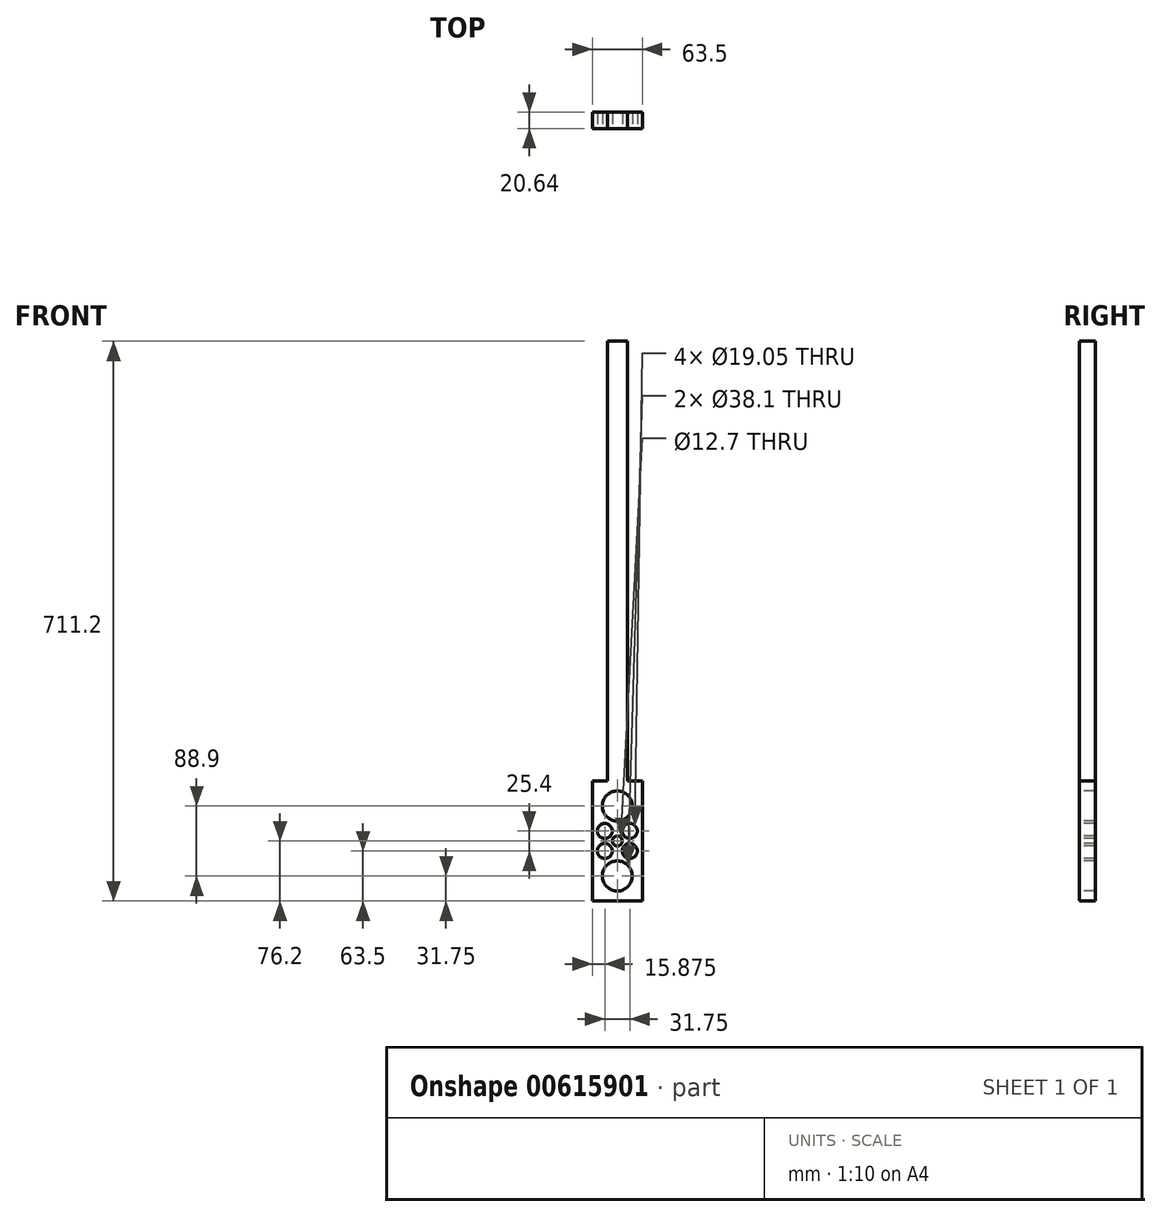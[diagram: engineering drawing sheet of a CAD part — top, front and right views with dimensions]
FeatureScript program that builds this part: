
annotation { "Feature Type Name" : "Feature", "Feature Type Description" : "" }
export const myFeature = defineFeature(function(context is Context, id is Id, definition is map)
    precondition{}
    {
        {
            var Q0;
            Q0=qCreatedBy(makeId("Front.planeOp"),FACE);
            var sketch = newSketch(context, id + "F0", { "sketchPlane" : qUnion([Q0])});
            skLineSegment(sketch, "E0.bottom", {"start": v(0, 0) * mm, "end": v(-63.5, 0) * mm});
            skLineSegment(sketch, "E0.top", {"start": v(0, 152.4) * mm, "end": v(-63.5, 152.4) * mm});
            skLineSegment(sketch, "E0.left", {"start": v(0, 0) * mm, "end": v(0, 152.4) * mm});
            skLineSegment(sketch, "E0.right", {"start": v(-63.5, 0) * mm, "end": v(-63.5, 152.4) * mm});
            skLineSegment(sketch, "E1.bottom", {"start": v(-31.75, 152.4) * mm, "end": v(-44.45, 152.4) * mm});
            skLineSegment(sketch, "E1.top", {"start": v(-31.75, 711.2) * mm, "end": v(-44.45, 711.2) * mm});
            skLineSegment(sketch, "E1.left", {"start": v(-31.75, 152.4) * mm, "end": v(-31.75, 711.2) * mm});
            skLineSegment(sketch, "E1.right", {"start": v(-44.45, 152.4) * mm, "end": v(-44.45, 711.2) * mm});
            skLineSegment(sketch, "E2.bottom", {"start": v(-31.75, 152.4) * mm, "end": v(-19.05, 152.4) * mm});
            skLineSegment(sketch, "E2.top", {"start": v(-31.75, 711.2) * mm, "end": v(-19.05, 711.2) * mm});
            skLineSegment(sketch, "E2.right", {"start": v(-19.05, 152.4) * mm, "end": v(-19.05, 711.2) * mm});
            skSolve(sketch);
        }
        {
            var Q0;
            Q0 = qSketchRegion(id + "F0", true);
            extrude(context, id + "F1", {"entities" : qUnion([Q0]), "depth" : 20.64 * mm, "offsetDistance" : 25.4 * mm});
        }
        {
            var Q0;
            Q0=makeQuery(id+"F1.opExtrude","CAP_FACE",FACE,{"disambiguationData":[OSD([sQuery(id+"F0.wireOp",EDGE,"E0.bottom"),sQuery(id+"F0.wireOp",EDGE,"E0.top"),sQuery(id+"F0.wireOp",EDGE,"E0.left"),sQuery(id+"F0.wireOp",EDGE,"E0.right"),sQuery(id+"F0.wireOp",EDGE,"E1.top"),sQuery(id+"F0.wireOp",EDGE,"E1.right"),sQuery(id+"F0.wireOp",EDGE,"E2.top"),sQuery(id+"F0.wireOp",EDGE,"E2.right")])],"isStart":false});
            var sketch = newSketch(context, id + "F2", { "sketchPlane" : qUnion([Q0])});
            skLineSegment(sketch, "E3", {"start": v(0, 0) * mm, "end": v(-31.75, 0) * mm});
            skLineSegment(sketch, "E4", {"start": v(-31.75, 0) * mm, "end": v(-31.75, 31.75) * mm, "construction": true});
            skCircle(sketch, "E5", {"center": v(-31.75, 31.75) * mm, "radius": 19.05 * mm});
            skLineSegment(sketch, "E6", {"start": v(0, 0) * mm, "end": v(-15.88, 0) * mm});
            skLineSegment(sketch, "E7", {"start": v(-15.88, 0) * mm, "end": v(-15.88, 63.5) * mm, "construction": true});
            skLineSegment(sketch, "E8", {"start": v(-63.5, 0) * mm, "end": v(-47.62, 0) * mm});
            skLineSegment(sketch, "E9", {"start": v(-47.62, 0) * mm, "end": v(-47.62, 63.5) * mm, "construction": true});
            skCircle(sketch, "E10", {"center": v(-47.63, 63.5) * mm, "radius": 9.53 * mm});
            skCircle(sketch, "E11", {"center": v(-15.88, 63.5) * mm, "radius": 9.53 * mm});
            skLineSegment(sketch, "E12", {"start": v(-63.5, 0) * mm, "end": v(-55.56, 0) * mm});
            skLineSegment(sketch, "E13", {"start": v(0, 0) * mm, "end": v(-7.94, 0) * mm});
            skLineSegment(sketch, "E14", {"start": v(-31.75, 0) * mm, "end": v(-23.81, 0) * mm});
            skLineSegment(sketch, "E15", {"start": v(-31.75, 0) * mm, "end": v(-39.69, 0) * mm});
            skLineSegment(sketch, "E16", {"start": v(-63.5, 0) * mm, "end": v(-42.33, 0) * mm});
            skLineSegment(sketch, "E17", {"start": v(0, 0) * mm, "end": v(-21.17, 0) * mm});
            skLineSegment(sketch, "E18", {"start": v(-31.75, 0) * mm, "end": v(-31.75, 57.15) * mm, "construction": true});
            skLineSegment(sketch, "E19", {"start": v(0, 0) * mm, "end": v(0, 76.2) * mm});
            skLineSegment(sketch, "E20", {"start": v(0, 76.2) * mm, "end": v(-63.5, 76.2) * mm});
            skCircle(sketch, "E21.MirrorC", {"center": v(-47.63, 88.9) * mm, "radius": 9.53 * mm});
            skCircle(sketch, "E22.MirrorC", {"center": v(-15.88, 88.9) * mm, "radius": 9.53 * mm});
            skCircle(sketch, "E23.MirrorC", {"center": v(-31.75, 120.65) * mm, "radius": 19.05 * mm});
            skCircle(sketch, "E24", {"center": v(-31.75, 76.2) * mm, "radius": 6.35 * mm});
            skSolve(sketch);
        }
        {
            var Q0;
            Q0 = qSketchRegion(id + "F2", true);
            extrude(context, id + "F3", {"entities" : qUnion([Q0]), "operationType" : NewBodyOperationType.REMOVE, "oppositeDirection" : true, "depth" : 25.4 * mm, "offsetDistance" : 25.4 * mm});
        }
    });
